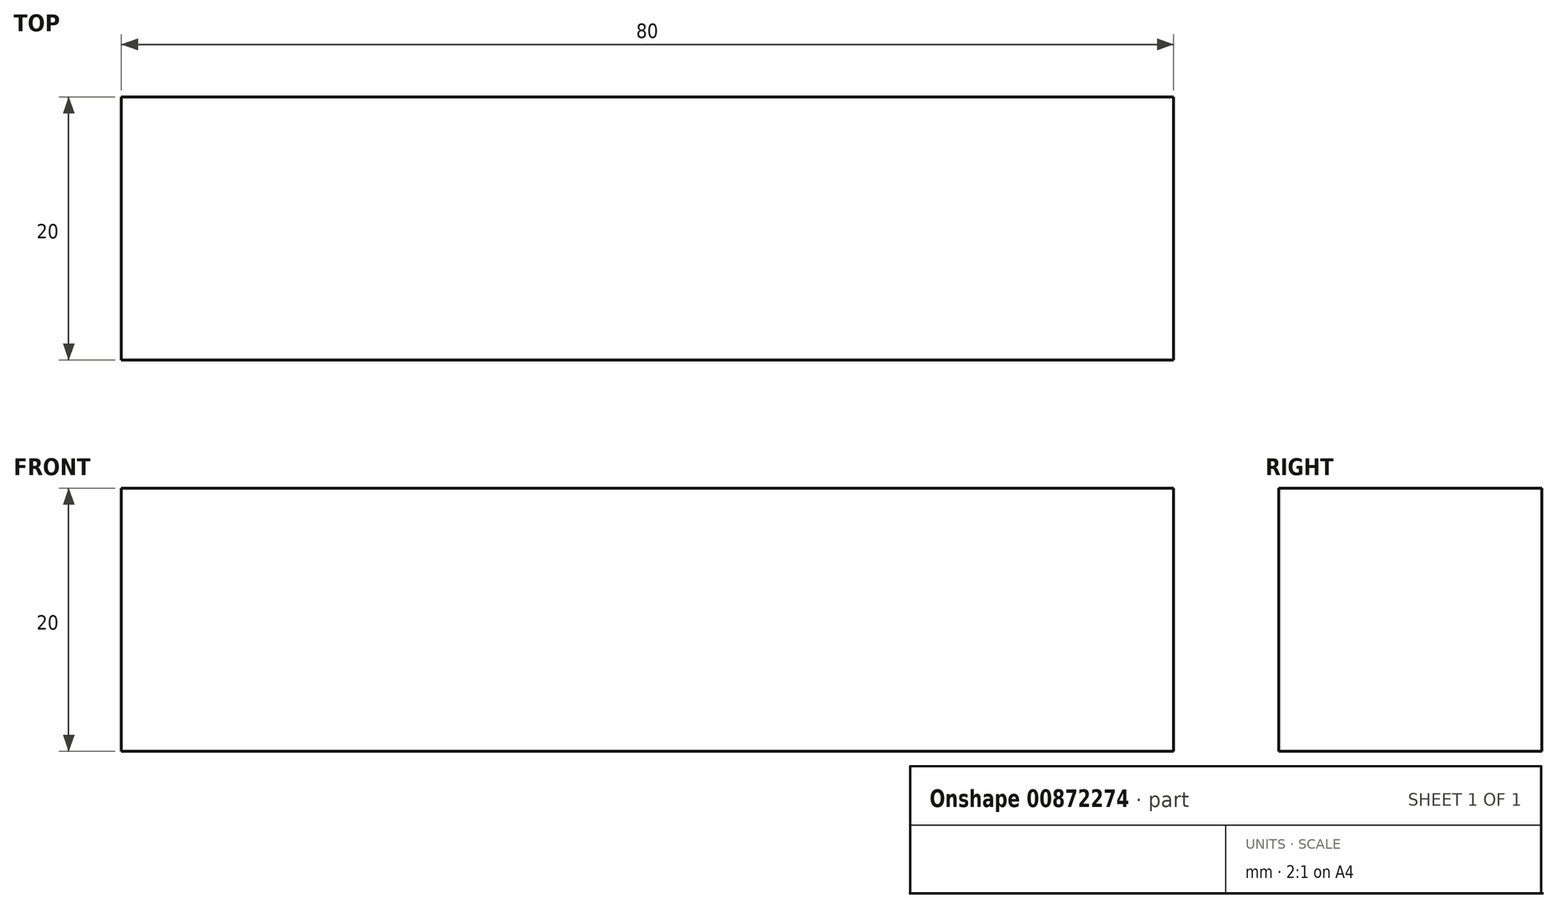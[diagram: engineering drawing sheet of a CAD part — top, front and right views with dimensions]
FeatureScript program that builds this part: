
annotation { "Feature Type Name" : "Feature", "Feature Type Description" : "" }
export const myFeature = defineFeature(function(context is Context, id is Id, definition is map)
    precondition{}
    {
        {
            var Q0;
            Q0=qCreatedBy(makeId("Front.planeOp"),FACE);
            var sketch = newSketch(context, id + "F0", { "sketchPlane" : qUnion([Q0])});
            skLineSegment(sketch, "E0.bottom", {"start": v(40, -10) * mm, "end": v(-40, -10) * mm});
            skLineSegment(sketch, "E0.top", {"start": v(40, 10) * mm, "end": v(-40, 10) * mm});
            skLineSegment(sketch, "E0.left", {"start": v(40, -10) * mm, "end": v(40, 10) * mm});
            skLineSegment(sketch, "E0.right", {"start": v(-40, -10) * mm, "end": v(-40, 10) * mm});
            skPoint(sketch, "E0.middle", {"position": v(0, 0) * mm});
            skSolve(sketch);
        }
        {
            var Q0;
            Q0=makeQuery(id+"F0.imprint","IMPRINT",FACE,{"disambiguationData":[TD([[makeQuery(id+"F0.imprint","IMPRINT",EDGE,{"derivedFrom":sQuery(id+"F0.wireOp",EDGE,"E0.bottom")}),-1.0]])]});
            extrude(context, id + "F1", {"entities" : qUnion([Q0]), "endBound" : BoundingType.SYMMETRIC, "depth" : 20 * mm, "offsetDistance" : 25 * mm});
        }
    });
